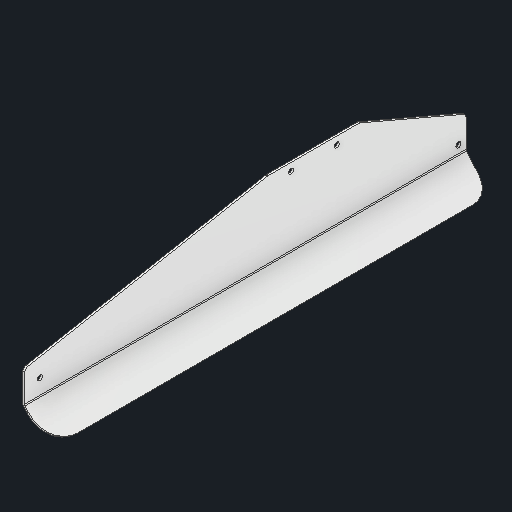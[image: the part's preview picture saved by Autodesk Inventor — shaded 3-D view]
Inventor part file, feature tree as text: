
AUTODESK INVENTOR PART (.ipt)
format: ipt  version: 2025 (Build 290162000, 162)  size: 135,680 bytes
history: native  units: in
note: dims shown in document units (in); Inventor stores cm internally (conversion verified against a paired STEP export)
features: other x4, sketch x1, extrude x1
ambient origin geometry x8: Origin, YZ Plane, XZ Plane, XY Plane, X Axis, Y Axis, Z Axis, Center Point
bodies: Solid1 (feature_tree)
feature tree (6):
  other  "Blocks"
  sketch  "Sketch1"  dims[d0=1.0in d1=0.125in d2=0.125in d3=0.125in d4=1.25in d5=90.0deg d6=1.0in d7=0.5in d8=0.0625in d9=0.0in d10=0.125in d11=0.2749in]
  extrude  "Extrusion1"  Depth=0.0625in TaperAngle=0.0deg
  other  "Bend Part1"
  other  "main"
  other  "main:1"
